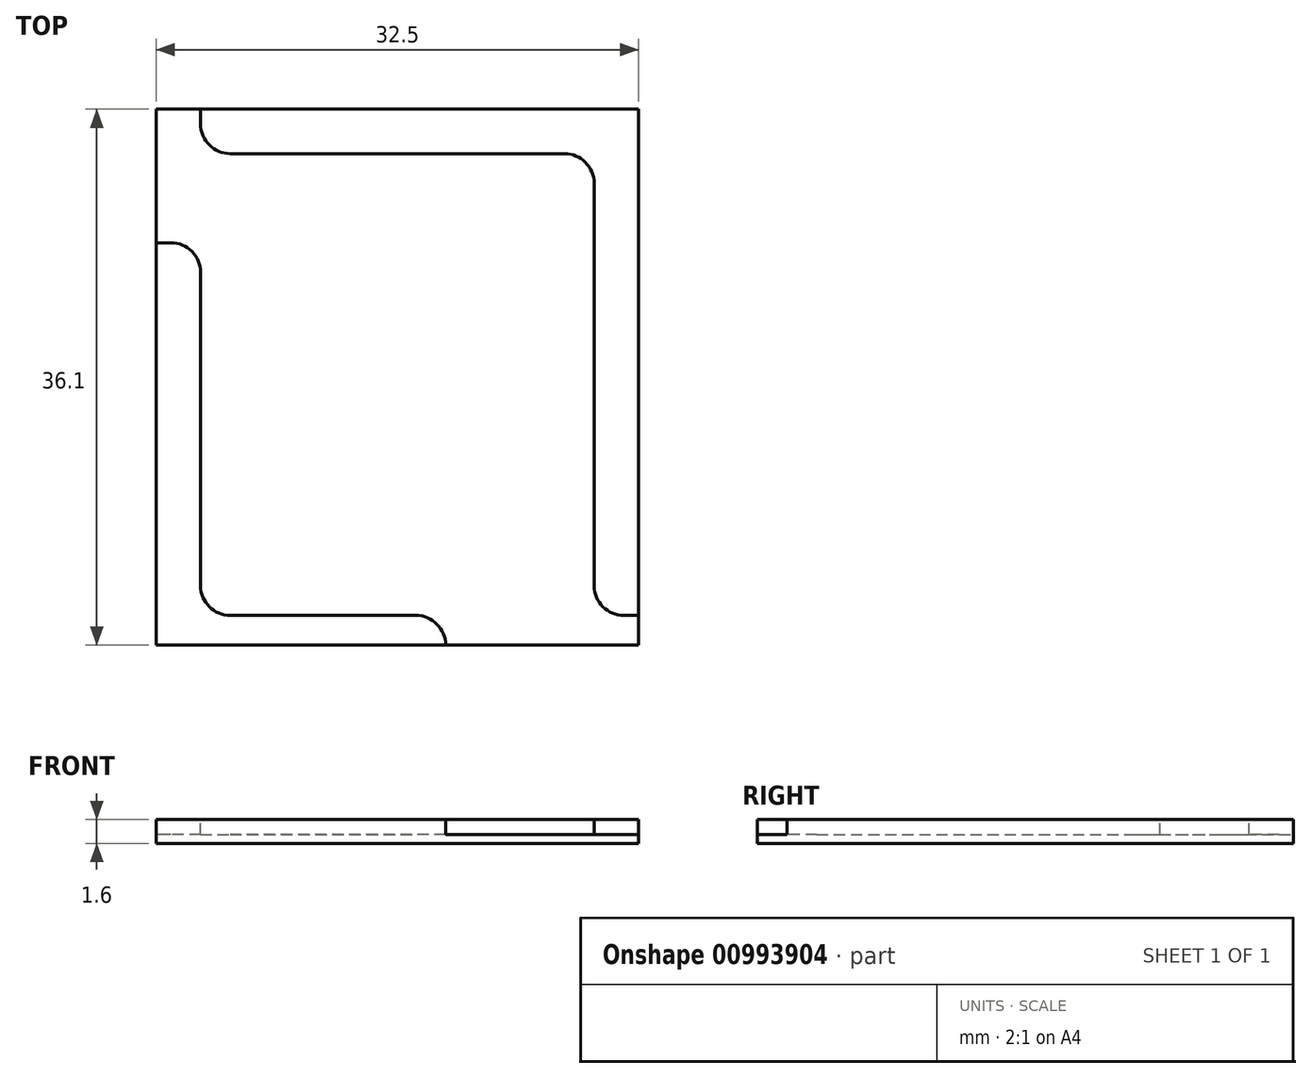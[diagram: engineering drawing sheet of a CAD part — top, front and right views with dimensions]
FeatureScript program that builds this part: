
annotation { "Feature Type Name" : "Feature", "Feature Type Description" : "" }
export const myFeature = defineFeature(function(context is Context, id is Id, definition is map)
    precondition{}
    {
        {
            var Q0;
            Q0=qCreatedBy(makeId("Top.planeOp"),FACE);
            var sketch = newSketch(context, id + "F0", { "sketchPlane" : qUnion([Q0])});
            skLineSegment(sketch, "E0.bottom", {"start": v(0, 0) * mm, "end": v(-32.5, 0) * mm});
            skLineSegment(sketch, "E0.top", {"start": v(0, 36.1) * mm, "end": v(-32.5, 36.1) * mm});
            skLineSegment(sketch, "E0.left", {"start": v(0, 0) * mm, "end": v(0, 36.1) * mm});
            skLineSegment(sketch, "E0.right", {"start": v(-32.5, 0) * mm, "end": v(-32.5, 36.1) * mm});
            skSolve(sketch);
        }
        {
            var Q0;
            Q0=makeQuery(id+"F0.imprint","IMPRINT",FACE,{"disambiguationData":[TD([[makeQuery(id+"F0.imprint","IMPRINT",EDGE,{"derivedFrom":sQuery(id+"F0.wireOp",EDGE,"E0.bottom")}),-1.0]])]});
            extrude(context, id + "F1", {"entities" : qUnion([Q0]), "depth" : 9.6 * mm, "offsetDistance" : 25 * mm});
        }
        {
            var Q0;
            Q0=makeQuery(id+"F1.opExtrude","CAP_FACE",FACE,{"disambiguationData":[OSD([sQuery(id+"F0.wireOp",EDGE,"E0.bottom"),sQuery(id+"F0.wireOp",EDGE,"E0.top"),sQuery(id+"F0.wireOp",EDGE,"E0.left"),sQuery(id+"F0.wireOp",EDGE,"E0.right")])],"isStart":false});
            var sketch = newSketch(context, id + "F2", { "sketchPlane" : qUnion([Q0])});
            skLineSegment(sketch, "E1.0", {"start": v(-3, 4) * mm, "end": v(-3, 31.1) * mm});
            skLineSegment(sketch, "E2.0", {"start": v(-29.5, 4) * mm, "end": v(-29.5, 25.1) * mm});
            skLineSegment(sketch, "E3", {"start": v(-31.5, 27.1) * mm, "end": v(-32.5, 27.1) * mm});
            skLineSegment(sketch, "E4", {"start": v(-32.5, 0) * mm, "end": v(-13, 0) * mm});
            skLineSegment(sketch, "E5.0", {"start": v(-27.5, 2) * mm, "end": v(-15, 2) * mm});
            skLineSegment(sketch, "E6", {"start": v(-13, 0) * mm, "end": v(-13, 0) * mm});
            skLineSegment(sketch, "E7.0", {"start": v(-5, 33.1) * mm, "end": v(-27.5, 33.1) * mm});
            skLineSegment(sketch, "E8", {"start": v(-29.5, 35.1) * mm, "end": v(-29.5, 36.1) * mm});
            skLineSegment(sketch, "E9", {"start": v(-1, 2) * mm, "end": v(0, 2) * mm});
            skPoint(sketch, "E10.visualSharp", {"position": v(-29.5, 27.1) * mm});
            skArc(sketch, "E10.filletArc", {"start": v(-29.5, 25.1) * mm, "mid": v(-30.09, 26.51) * mm, "end": v(-31.5, 27.1) * mm});
            skPoint(sketch, "E11.visualSharp", {"position": v(-13, 2) * mm});
            skArc(sketch, "E11.filletArc", {"start": v(-13, 0) * mm, "mid": v(-13.59, 1.41) * mm, "end": v(-15, 2) * mm});
            skPoint(sketch, "E12.visualSharp", {"position": v(-3, 2) * mm});
            skArc(sketch, "E12.filletArc", {"start": v(-3, 4) * mm, "mid": v(-2.41, 2.59) * mm, "end": v(-1, 2) * mm});
            skPoint(sketch, "E13.visualSharp", {"position": v(-29.5, 33.1) * mm});
            skArc(sketch, "E13.filletArc", {"start": v(-29.5, 35.1) * mm, "mid": v(-28.91, 33.69) * mm, "end": v(-27.5, 33.1) * mm});
            skPoint(sketch, "E14.visualSharp", {"position": v(-29.5, 2) * mm});
            skArc(sketch, "E14.filletArc", {"start": v(-29.5, 4) * mm, "mid": v(-28.91, 2.59) * mm, "end": v(-27.5, 2) * mm});
            skPoint(sketch, "E15.visualSharp", {"position": v(-3, 33.1) * mm});
            skArc(sketch, "E15.filletArc", {"start": v(-3, 31.1) * mm, "mid": v(-3.59, 32.51) * mm, "end": v(-5, 33.1) * mm});
            skSolve(sketch);
        }
        {
            var Q0;
            Q0=makeQuery(id+"F2.imprint","IMPRINT",FACE,{"disambiguationData":[TD([[makeQuery(id+"F2.imprint","IMPRINT",EDGE,{"derivedFrom":sQuery(id+"F2.wireOp",EDGE,"E2.0")}),1.0]])]});
            var Q1;
            Q1=makeQuery(id+"F2.imprint","IMPRINT",FACE,{"disambiguationData":[TD([[makeQuery(id+"F2.imprint","IMPRINT",EDGE,{"derivedFrom":sQuery(id+"F2.wireOp",EDGE,"E1.0")}),-1.0]])]});
            extrude(context, id + "F3", {"entities" : qUnion([Q0, Q1]), "operationType" : NewBodyOperationType.REMOVE, "oppositeDirection" : true, "depth" : 8 * mm, "offsetDistance" : 25 * mm});
        }
        {
            var Q0;
            Q0=makeQuery(id+"F1.opExtrude","CAP_FACE",FACE,{"disambiguationData":[OSD([sQuery(id+"F0.wireOp",EDGE,"E0.bottom"),sQuery(id+"F0.wireOp",EDGE,"E0.top"),sQuery(id+"F0.wireOp",EDGE,"E0.left"),sQuery(id+"F0.wireOp",EDGE,"E0.right")])],"isStart":false});
            extrude(context, id + "F4", {"entities" : qUnion([Q0]), "operationType" : NewBodyOperationType.REMOVE, "oppositeDirection" : true, "depth" : 9 * mm, "offsetDistance" : 25 * mm});
        }
        {
            var Q0;
            Q0=qCreatedBy(makeId("Right.planeOp"),FACE);
            cPlane(context, id + "F5", {"entities" : qUnion([Q0]), "cplaneType" : CPlaneType.OFFSET, "offset" : 16.25 * mm, "oppositeDirection" : true, "width" : 150 * mm, "height" : 150 * mm});
        }
    });
